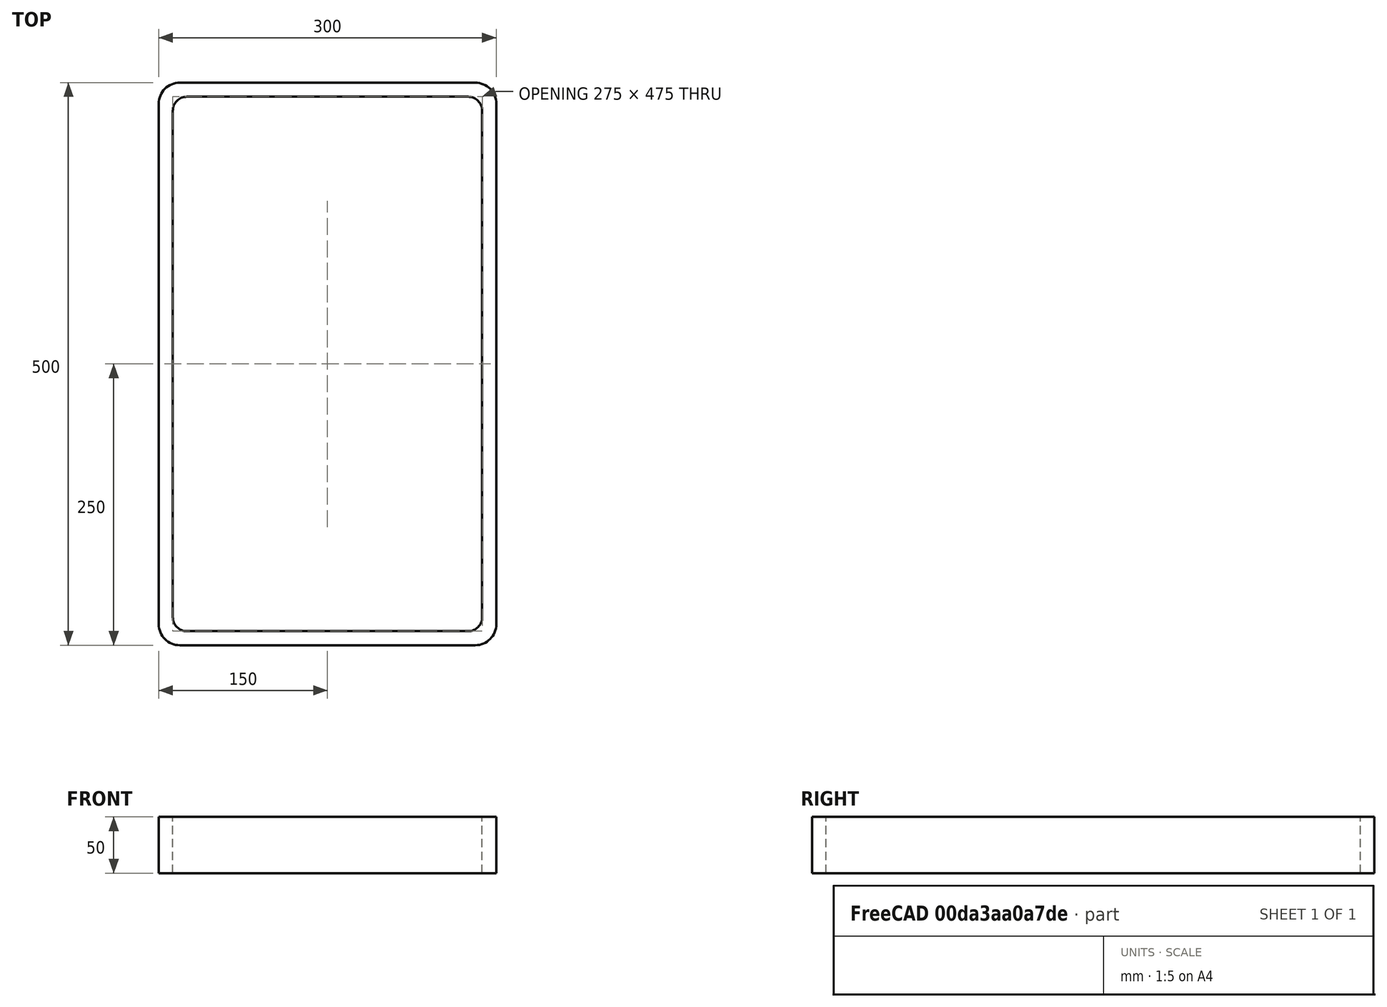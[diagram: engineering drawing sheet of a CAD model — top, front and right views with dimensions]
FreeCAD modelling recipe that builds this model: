
FCSTD DOCUMENT  (FreeCAD 0.15R4671 (Git))
Label: Rectangular hollow section 500x300x12.5 EN10219 S235JRH
License: All rights reserved
LicenseURL: http://en.wikipedia.org/wiki/All_rights_reserved
objects: Sketcher::SketchObject×1, Part::Extrusion×1
note: 2 computed .brp shape members not serialized (recipe doc carries the construction recipe); baked Part::Feature solids carry a one-line shape summary decoded from their .brp

FEATURE [Sketcher::SketchObject] Sketch
  sketch-geometry (16):
    g0: LineSegment StartX=-125 StartY=237.5 StartZ=0 EndX=125 EndY=237.5 EndZ=0
    g1: LineSegment StartX=137.5 StartY=225 StartZ=0 EndX=137.5 EndY=-225 EndZ=0
    g2: LineSegment StartX=125 StartY=-237.5 StartZ=0 EndX=-125 EndY=-237.5 EndZ=0
    g3: LineSegment StartX=-137.5 StartY=-225 StartZ=0 EndX=-137.5 EndY=225 EndZ=0
    g4: LineSegment StartX=-131.25 StartY=250 StartZ=0 EndX=131.25 EndY=250 EndZ=0
    g5: LineSegment StartX=150 StartY=231.25 StartZ=0 EndX=150 EndY=-231.25 EndZ=0
    g6: LineSegment StartX=131.25 StartY=-250 StartZ=0 EndX=-131.25 EndY=-250 EndZ=0
    g7: LineSegment StartX=-150 StartY=-231.25 StartZ=0 EndX=-150 EndY=231.25 EndZ=0
    g8: ArcOfCircle CenterX=-125 CenterY=225 CenterZ=0 NormalX=0 NormalY=0 NormalZ=1 Radius=12.5 StartAngle=1.5708 EndAngle=3.14159
    g9: ArcOfCircle CenterX=125 CenterY=225 CenterZ=0 NormalX=0 NormalY=0 NormalZ=1 Radius=12.5 StartAngle=0 EndAngle=1.5708
    g10: ArcOfCircle CenterX=125 CenterY=-225 CenterZ=0 NormalX=0 NormalY=0 NormalZ=1 Radius=12.5 StartAngle=4.71239 EndAngle=6.28319
    g11: ArcOfCircle CenterX=-125 CenterY=-225 CenterZ=0 NormalX=0 NormalY=0 NormalZ=1 Radius=12.5 StartAngle=3.14159 EndAngle=4.71239
    g12: ArcOfCircle CenterX=131.25 CenterY=231.25 CenterZ=0 NormalX=0 NormalY=0 NormalZ=1 Radius=18.75 StartAngle=0 EndAngle=1.5708
    g13: ArcOfCircle CenterX=131.25 CenterY=-231.25 CenterZ=0 NormalX=0 NormalY=0 NormalZ=1 Radius=18.75 StartAngle=4.71239 EndAngle=6.28319
    g14: ArcOfCircle CenterX=-131.25 CenterY=-231.25 CenterZ=0 NormalX=0 NormalY=0 NormalZ=1 Radius=18.75 StartAngle=3.14159 EndAngle=4.71239
    g15: ArcOfCircle CenterX=-131.25 CenterY=231.25 CenterZ=0 NormalX=0 NormalY=0 NormalZ=1 Radius=18.75 StartAngle=1.5708 EndAngle=3.14159
  constraints (36):
    c: Horizontal(g2)
    c: Vertical(g3)
    c: Horizontal(g6)
    c: Vertical(g7)
    c: Tangent(g3,g8) = 1.5708
    c: Tangent(g0,g8) = 1.5708
    c: Tangent(g0,g9) = 1.5708
    c: Tangent(g1,g9) = 1.5708
    c: Tangent(g1,g10) = 1.5708
    c: Tangent(g2,g10) = 1.5708
    c: Tangent(g2,g11) = 1.5708
    c: Tangent(g3,g11) = 1.5708
    c: Tangent(g4,g12) = 1.5708
    c: Tangent(g5,g12) = 1.5708
    c: Tangent(g5,g13) = 1.5708
    c: Tangent(g6,g13) = 1.5708
    c: Tangent(g6,g14) = 1.5708
    c: Tangent(g7,g14) = 1.5708
    c: Tangent(g7,g15) = 1.5708
    c: Tangent(g4,g15) = 1.5708
    c: Equal(g9,g8)
    c: Equal(g9,g11)
    c: Equal(g9,g10)
    c: Equal(g12,g15)
    c: Equal(g12,g14)
    c: Equal(g12,g13)
    c: Symmetric(g4,g6,g-1)
    c: Symmetric(g7,g5,g-2)
    c: DistanceY(g4,g6) = -500
    c: DistanceX(g7,g5) = 300
    c: Symmetric(g3,g1,g-2)
    c: Symmetric(g0,g2,g-1)
    c: DistanceY(g0,g4) = 12.5
    c: DistanceX(g5,g1) = -12.5
    c: Radius(g9) = 12.5
    c: Radius(g12) = 18.75
FEATURE [Part::Extrusion] Extrude  label="Rectangular hollow section 500x300x12.5 EN10219 S235JRH"
  Base = -> Sketch
  Dir = (0,0,50)
  Solid = true
